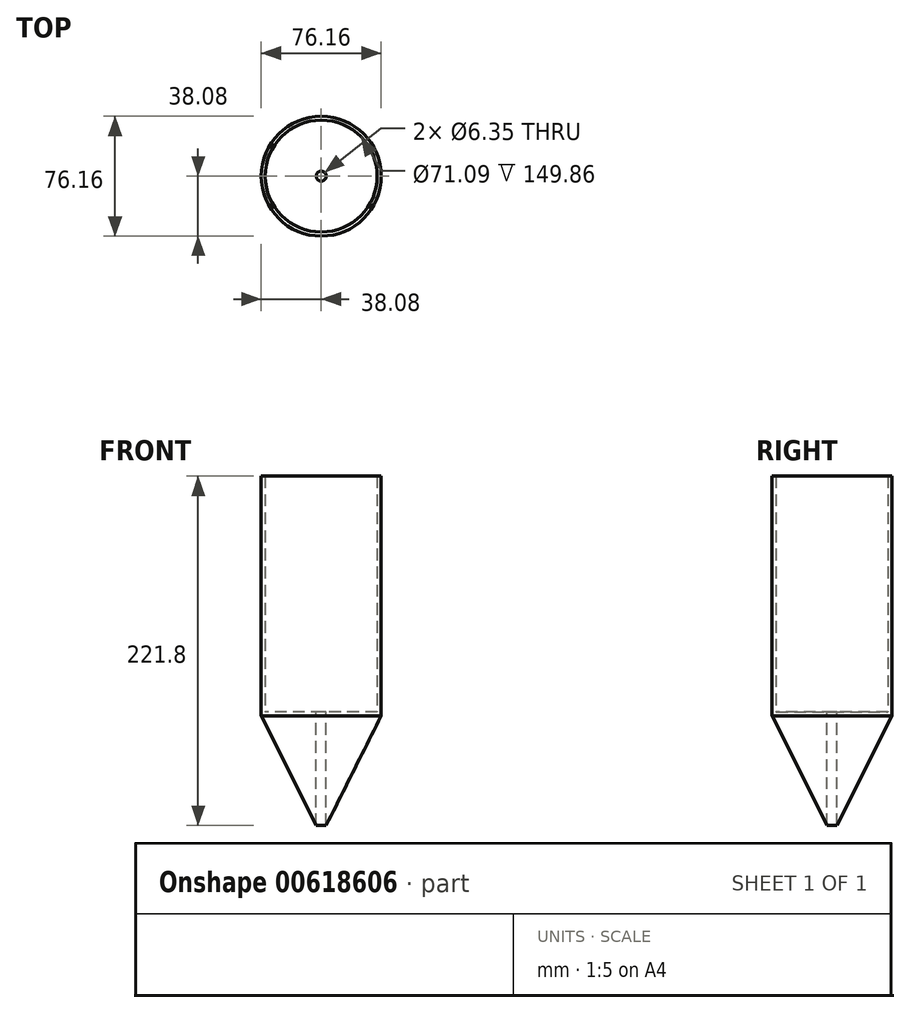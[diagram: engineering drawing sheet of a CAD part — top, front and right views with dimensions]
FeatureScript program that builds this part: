
annotation { "Feature Type Name" : "Feature", "Feature Type Description" : "" }
export const myFeature = defineFeature(function(context is Context, id is Id, definition is map)
    precondition{}
    {
        {
            var Q0;
            Q0=qCreatedBy(makeId("Top.planeOp"),FACE);
            var sketch = newSketch(context, id + "F0", { "sketchPlane" : qUnion([Q0])});
            skCircle(sketch, "E0", {"center": v(0, 0) * mm, "radius": 38.08 * mm});
            skSolve(sketch);
        }
        {
            var Q0;
            Q0=makeQuery(id+"F0.imprint","IMPRINT",FACE,{"disambiguationData":[TD([[makeQuery(id+"F0.imprint","IMPRINT",EDGE,{"derivedFrom":sQuery(id+"F0.wireOp",EDGE,"E0")}),1.0]])]});
            extrude(context, id + "F1", {"entities" : qUnion([Q0]), "depth" : 152.4 * mm, "offsetDistance" : 25.4 * mm});
        }
        {
            var Q0;
            Q0=makeQuery(id+"F1.opExtrude","CAP_FACE",FACE,{"disambiguationData":[OSD([sQuery(id+"F0.wireOp",EDGE,"E0")])],"isStart":false});
            var sketch = newSketch(context, id + "F2", { "sketchPlane" : qUnion([Q0])});
            skCircle(sketch, "E1", {"center": v(0, 0) * mm, "radius": 27.53 * mm});
            skSolve(sketch);
        }
        {
            var Q0;
            Q0=makeQuery(id+"F1.opExtrude","CAP_FACE",FACE,{"disambiguationData":[OSD([sQuery(id+"F0.wireOp",EDGE,"E0")])],"isStart":false});
            shell(context, id + "F3", {"entities" : qUnion([Q0]), "thickness" : 2.54 * mm});
        }
        {
            var Q0;
            Q0=qCreatedBy(makeId("Right.planeOp"),FACE);
            var sketch = newSketch(context, id + "F4", { "sketchPlane" : qUnion([Q0])});
            skLineSegment(sketch, "E2", {"start": v(0, 0) * mm, "end": v(0, -75.72) * mm});
            skLineSegment(sketch, "E3", {"start": v(0, -75.72) * mm, "end": v(-38.04, 0) * mm});
            skLineSegment(sketch, "E4", {"start": v(-38.04, 0) * mm, "end": v(0, 0) * mm});
            skSolve(sketch);
        }
        {
            var Q0;
            Q0=makeQuery(id+"F4.imprint","IMPRINT",FACE,{"disambiguationData":[TD([[makeQuery(id+"F4.imprint","IMPRINT",EDGE,{"derivedFrom":sQuery(id+"F4.wireOp",EDGE,"E2")}),-1.0]])]});
            var Q1;
            Q1=sQuery(id+"F4.wireOp",EDGE,"E2");
            revolve(context, id + "F5", {"entities" : qUnion([Q0]), "axis" : qUnion([Q1]), "revolveType" : RevolveType.FULL});
        }
        {
            var Q0;
            Q0=sQuery(id+"F2.wireOp",VERTEX,"E1.center");
            var Q1;
            Q1=makeQuery(id+"F1.opExtrude","SWEPT_BODY",BODY,{"disambiguationData":[OSD([sQuery(id+"F0.wireOp",EDGE,"E0")])]});
            var Q2;
            Q2=makeQuery(id+"F5.opRevolve","SWEPT_BODY",BODY,{"disambiguationData":[OSD([sQuery(id+"F4.wireOp",EDGE,"E2"),sQuery(id+"F4.wireOp",EDGE,"E3"),sQuery(id+"F4.wireOp",EDGE,"E4")])]});
            hole(context, id + "F6", {"style" : HoleStyle.SIMPLE, "endStyle" : HoleEndStyle.THROUGH, "holeDiameter" : 6.35 * mm, "majorDiameter" : 6.35 * mm, "isTappedThrough" : true, "tappedDepth" : 12.7 * mm, "tapClearance" : 3, "locations" : qUnion([Q0]), "scope" : qUnion([Q1, Q2])});
        }
    });
